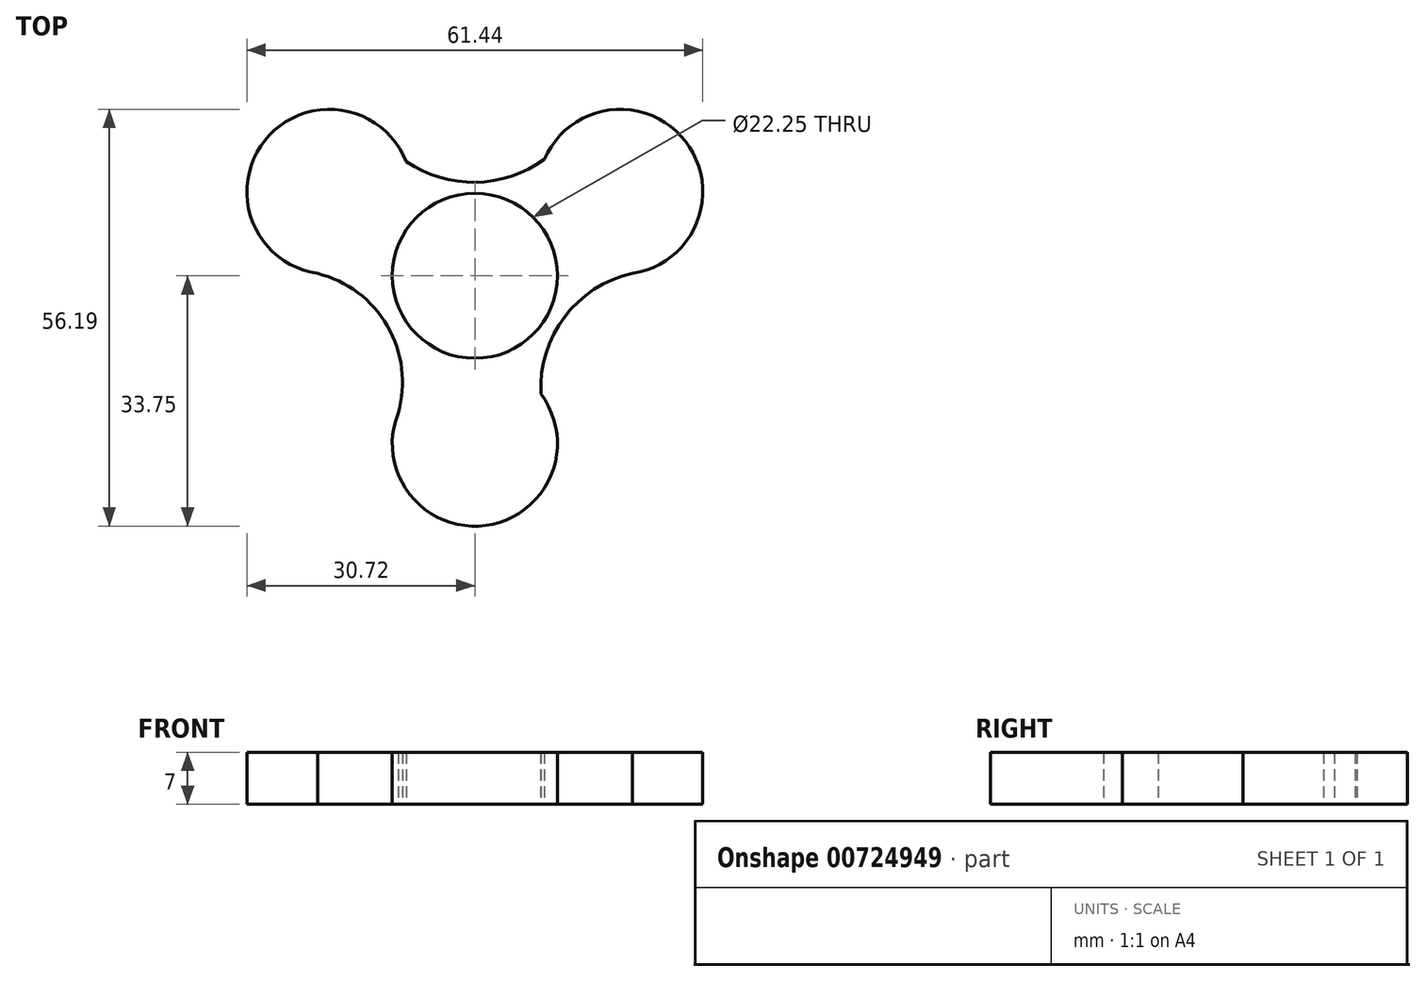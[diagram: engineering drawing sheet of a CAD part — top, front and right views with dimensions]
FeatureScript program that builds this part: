
annotation { "Feature Type Name" : "Feature", "Feature Type Description" : "" }
export const myFeature = defineFeature(function(context is Context, id is Id, definition is map)
    precondition{}
    {
        {
            var Q0;
            Q0=qCreatedBy(makeId("Top.planeOp"),FACE);
            var sketch = newSketch(context, id + "F0", { "sketchPlane" : qUnion([Q0])});
            skCircle(sketch, "E0", {"center": v(0, 0) * mm, "radius": 11.12 * mm});
            skCircle(sketch, "E1", {"center": v(0, -22.63) * mm, "radius": 11.12 * mm});
            skCircle(sketch, "E2.1.0", {"center": v(19.6, 11.31) * mm, "radius": 11.12 * mm});
            skCircle(sketch, "E2.2.0", {"center": v(-19.6, 11.31) * mm, "radius": 11.12 * mm});
            skArc(sketch, "E3", {"start": v(-2.04, -33.56) * mm, "mid": v(0, -33.63) * mm, "end": v(2.04, -33.56) * mm});
            skArc(sketch, "E4.trimOffspring", {"start": v(-28.05, 18.55) * mm, "mid": v(-29.12, 16.81) * mm, "end": v(-30.09, 15.02) * mm});
            skArc(sketch, "E5.trimOffspring", {"start": v(30.09, 15.02) * mm, "mid": v(29.12, 16.81) * mm, "end": v(28.05, 18.55) * mm});
            skCircle(sketch, "E6", {"center": v(0, 0) * mm, "radius": 4.05 * mm});
            skArc(sketch, "E7", {"start": v(-10.73, -19.7) * mm, "mid": v(-11.47, -7.33) * mm, "end": v(-21.22, 0.3) * mm});
            skArc(sketch, "E8", {"start": v(-9.25, 15.4) * mm, "mid": v(0.1, 12.61) * mm, "end": v(9.36, 15.67) * mm});
            skArc(sketch, "E9", {"start": v(21.22, 0.3) * mm, "mid": v(12.08, -5.57) * mm, "end": v(8.9, -15.95) * mm});
            skSolve(sketch);
        }
        {
            var Q0;
            Q0 = qSketchRegion(id + "F0", true);
            extrude(context, id + "F1", {"entities" : qUnion([Q0]), "depth" : 7 * mm, "offsetDistance" : 25 * mm});
        }
    });
